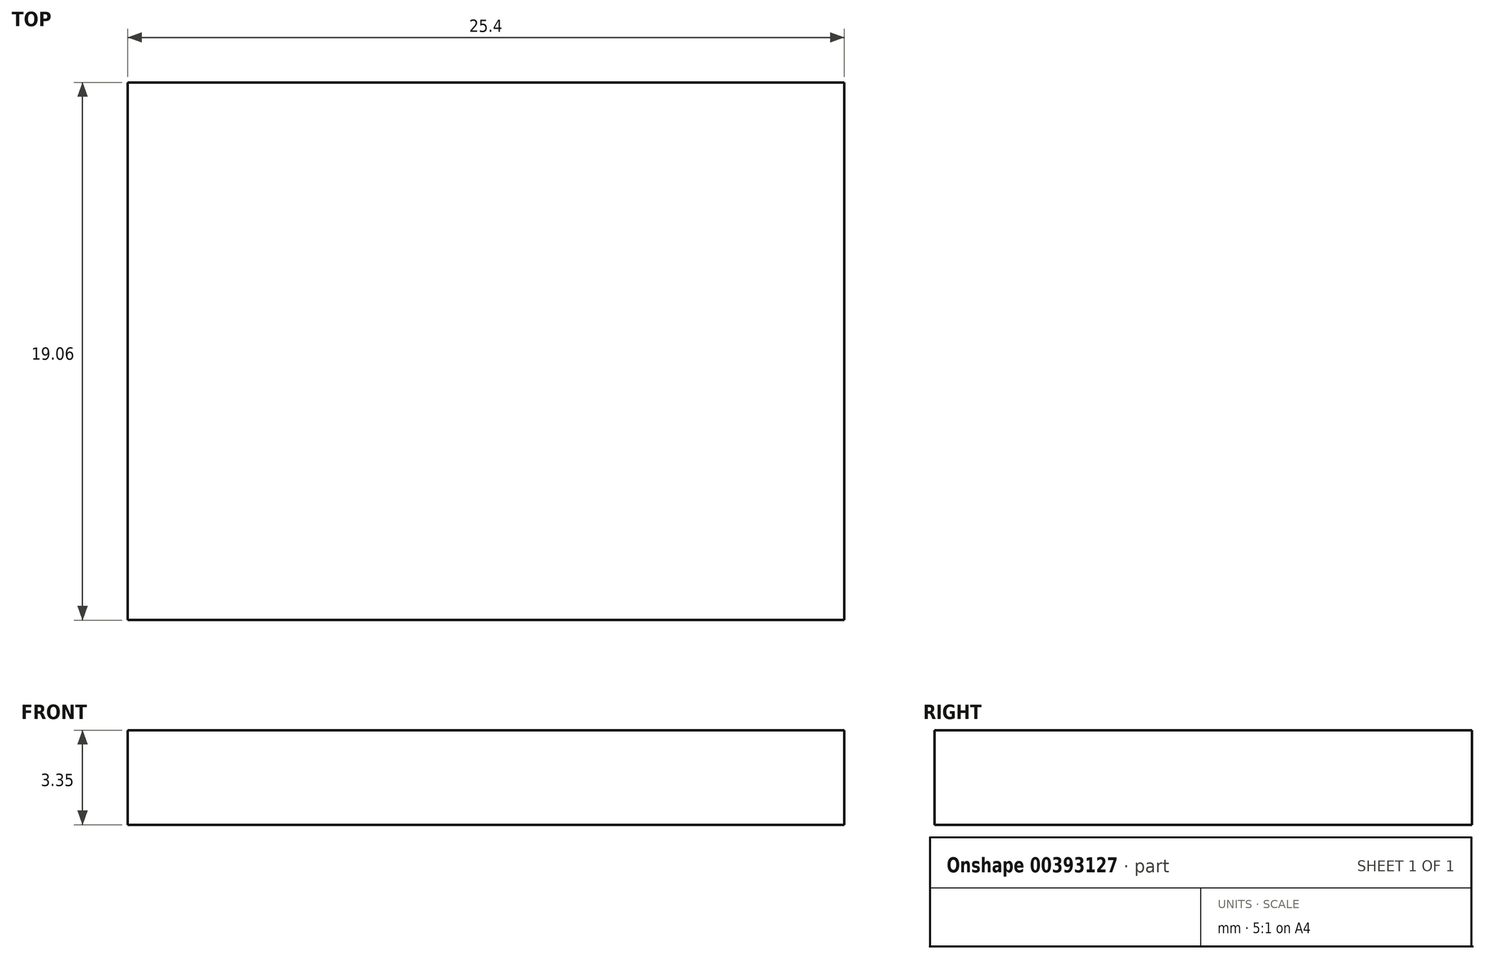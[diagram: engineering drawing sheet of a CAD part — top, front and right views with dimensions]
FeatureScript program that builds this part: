
annotation { "Feature Type Name" : "Feature", "Feature Type Description" : "" }
export const myFeature = defineFeature(function(context is Context, id is Id, definition is map)
    precondition{}
    {
        {
            var Q0;
            Q0=qCreatedBy(makeId("Top.planeOp"),FACE);
            var sketch = newSketch(context, id + "F0", { "sketchPlane" : qUnion([Q0])});
            skLineSegment(sketch, "E0.bottom", {"start": v(12.7, -9.53) * mm, "end": v(-12.7, -9.52) * mm});
            skLineSegment(sketch, "E0.top", {"start": v(12.7, 9.52) * mm, "end": v(-12.7, 9.53) * mm});
            skLineSegment(sketch, "E0.left", {"start": v(12.7, -9.53) * mm, "end": v(12.7, 9.53) * mm});
            skLineSegment(sketch, "E0.right", {"start": v(-12.7, -9.53) * mm, "end": v(-12.7, 9.53) * mm});
            skSolve(sketch);
        }
        {
            var Q0;
            Q0=makeQuery(id+"F0.imprint","IMPRINT",FACE,{"disambiguationData":[TD([[makeQuery(id+"F0.imprint","IMPRINT",EDGE,{"derivedFrom":sQuery(id+"F0.wireOp",EDGE,"E0.bottom")}),-1.0]])]});
            extrude(context, id + "F1", {"entities" : qUnion([Q0]), "depth" : 3.35 * mm});
        }
    });
